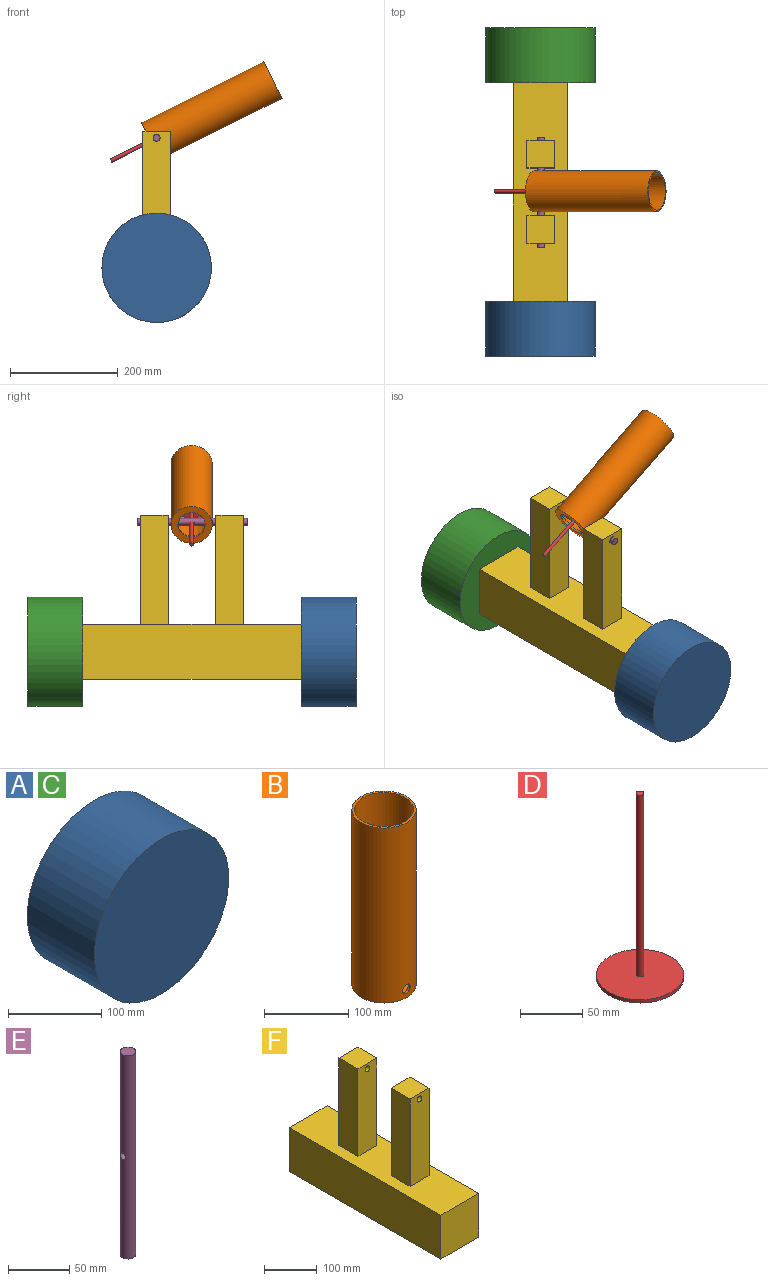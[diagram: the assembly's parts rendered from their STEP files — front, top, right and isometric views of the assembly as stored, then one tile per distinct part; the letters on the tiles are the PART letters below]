
ASSEMBLY  parts=6 mates=5
PART A: 3 faces, bbox 203.2x101.6x203.2 mm
  f0: cylinder r=101.6mm len=203.2mm, axis (0,1,0), area 64858.6mm2, adj f1,f2
  f1: plane 203.2x203.2mm, normal (0,-1,0), area 32429.3mm2, adj f0
  f2: plane 203.2x203.2mm, normal (0,1,0), area 32429.3mm2, adj f0
PART B: 8 faces, bbox 76.2x76.2x254 mm
  f0: cylinder r=38.1mm len=254mm, axis (0,0,-1), area 60549.3mm2, adj f2,f3,f6,f7
  f1: cylinder r=34.92mm len=250.19mm, axis (0,0,1), area 54646mm2, adj f2,f4,f6,f7
  f2: plane 76.2x76.2mm, normal (0,0,1), area 728.4mm2, adj f0,f1
  f3: plane 76.2x76.2mm, normal (0,0,-1), area 2533.5mm2, adj f0,f5
  f4: plane 69.85x69.85mm, normal (0,0,1), area 1805.1mm2, adj f1,f5
  f5: cylinder r=25.4mm len=50.8mm, axis (0,0,1), area 608mm2, adj f3,f4
  f6: cylinder r=6.35mm len=12.7mm, axis (0,1,0), area 127.6mm2, adj f0,f1
  f7: cylinder r=6.35mm len=12.7mm, axis (0,-1,0), area 127.7mm2, adj f0,f1
PART C: same geometry as A
PART D: 5 faces, bbox 69.9x69.9x181 mm
  f0: cylinder r=34.92mm len=69.85mm, axis (0,0,-1), area 696.7mm2, adj f1,f2
  f1: plane 69.85x69.85mm, normal (0,0,1), area 3800.3mm2, adj f0,f3
  f2: plane 69.85x69.85mm, normal (0,0,-1), area 3832mm2, adj f0
  f3: cylinder r=3.17mm len=177.8mm, axis (0,0,-1), area 3547mm2, adj f1,f4
  f4: plane 6.35x6.35mm, normal (0,0,1), area 31.7mm2, adj f3
PART E: 4 faces, bbox 12.7x12.7x203.2 mm
  f0: cylinder r=6.35mm len=203.2mm, axis (0,0,-1), area 8041.8mm2, adj f1,f2,f3
  f1: plane 12.7x12.7mm, normal (0,0,1), area 126.7mm2, adj f0
  f2: plane 12.7x12.7mm, normal (0,0,-1), area 126.7mm2, adj f0
  f3: cylinder r=3.17mm len=12.7mm, axis (1,0,0), area 236.7mm2, adj f0
PART F: 18 faces, bbox 101.6x406.4x304.8 mm
  f0: plane 406.4x101.6mm, normal (0,0,1), area 36129mm2, adj f1,f2,f3,f4,f6,f7,f8,f9
  f1: plane 101.6x101.6mm, normal (0,-1,0), area 10322.6mm2, adj f0,f2,f4,f5
  f2: plane 406.4x101.6mm, normal (1,0,0), area 41290.2mm2, adj f0,f1,f3,f5
  f3: plane 101.6x101.6mm, normal (0,1,0), area 10322.6mm2, adj f0,f2,f4,f5
  f4: plane 406.4x101.6mm, normal (-1,0,0), area 41290.2mm2, adj f0,f1,f3,f5
  f5: plane 406.4x101.6mm, normal (0,0,-1), area 41290.2mm2, adj f1,f2,f3,f4
  f6: plane 203.2x50.8mm, normal (0,-1,0), area 10195.9mm2, adj f0,f7,f9,f10,f17
  f7: plane 203.2x50.8mm, normal (1,0,0), area 10322.6mm2, adj f0,f6,f8,f10
  f8: plane 203.2x50.8mm, normal (0,1,0), area 10195.9mm2, adj f0,f7,f9,f10,f17
  f9: plane 203.2x50.8mm, normal (-1,0,0), area 10322.6mm2, adj f0,f6,f8,f10
  f10: plane 50.8x50.8mm, normal (0,0,1), area 2580.6mm2, adj f6,f7,f8,f9
  f11: plane 203.2x50.8mm, normal (0,-1,0), area 10195.9mm2, adj f0,f12,f14,f15,f16
  f12: plane 203.2x50.8mm, normal (1,0,0), area 10322.6mm2, adj f0,f11,f13,f15
  f13: plane 203.2x50.8mm, normal (0,1,0), area 10195.9mm2, adj f0,f12,f14,f15,f16
  f14: plane 203.2x50.8mm, normal (-1,0,0), area 10322.6mm2, adj f0,f11,f13,f15
  f15: plane 50.8x50.8mm, normal (0,0,1), area 2580.6mm2, adj f11,f12,f13,f14
  f16: cylinder r=6.35mm len=50.8mm, axis (0,-1,0), area 2026.8mm2, adj f11,f13
  f17: cylinder r=6.35mm len=50.8mm, axis (0,-1,0), area 2026.8mm2, adj f6,f8
PLACE A rot(axis=(0,-1,0),30.4deg) t=(1.23,-200.26,-32.82)mm
PLACE B rot(axis=(0,1,0),63.5deg) t=(-10.13,3.65,202.81)mm
PLACE C rot(axis=(0,1,0),167.6deg) t=(1.23,307.74,-32.82)mm
PLACE D rot(axis=(0.8,-0.33,-0.5),157.1deg) t=(78.85,3.65,247.21)mm
PLACE E rot(axis=(-0.21,0.69,0.69),155.9deg) t=(1.23,-99.83,208.48)mm fixed
PLACE F t=(1.23,2.94,-83.62)mm fixed
MATE revolute C.f0 <-> F.f3  axis (0,-1,0) through (1.23,206.14,-32.82)mm
MATE revolute B.f6 <-> E.f0  axis (0,1,0) through (1.23,39.87,208.48)mm
MATE revolute A.f0 <-> F.f1  axis (0,1,0) through (1.23,-200.26,-32.82)mm
MATE cylindrical D.f3 <-> B.f1  axis (0.89,0,0.45) through (-3.54,3.65,206.1)mm
MATE cylindrical E.f0 <-> F.f16  axis (0,-1,0) through (1.23,1.77,208.48)mm
